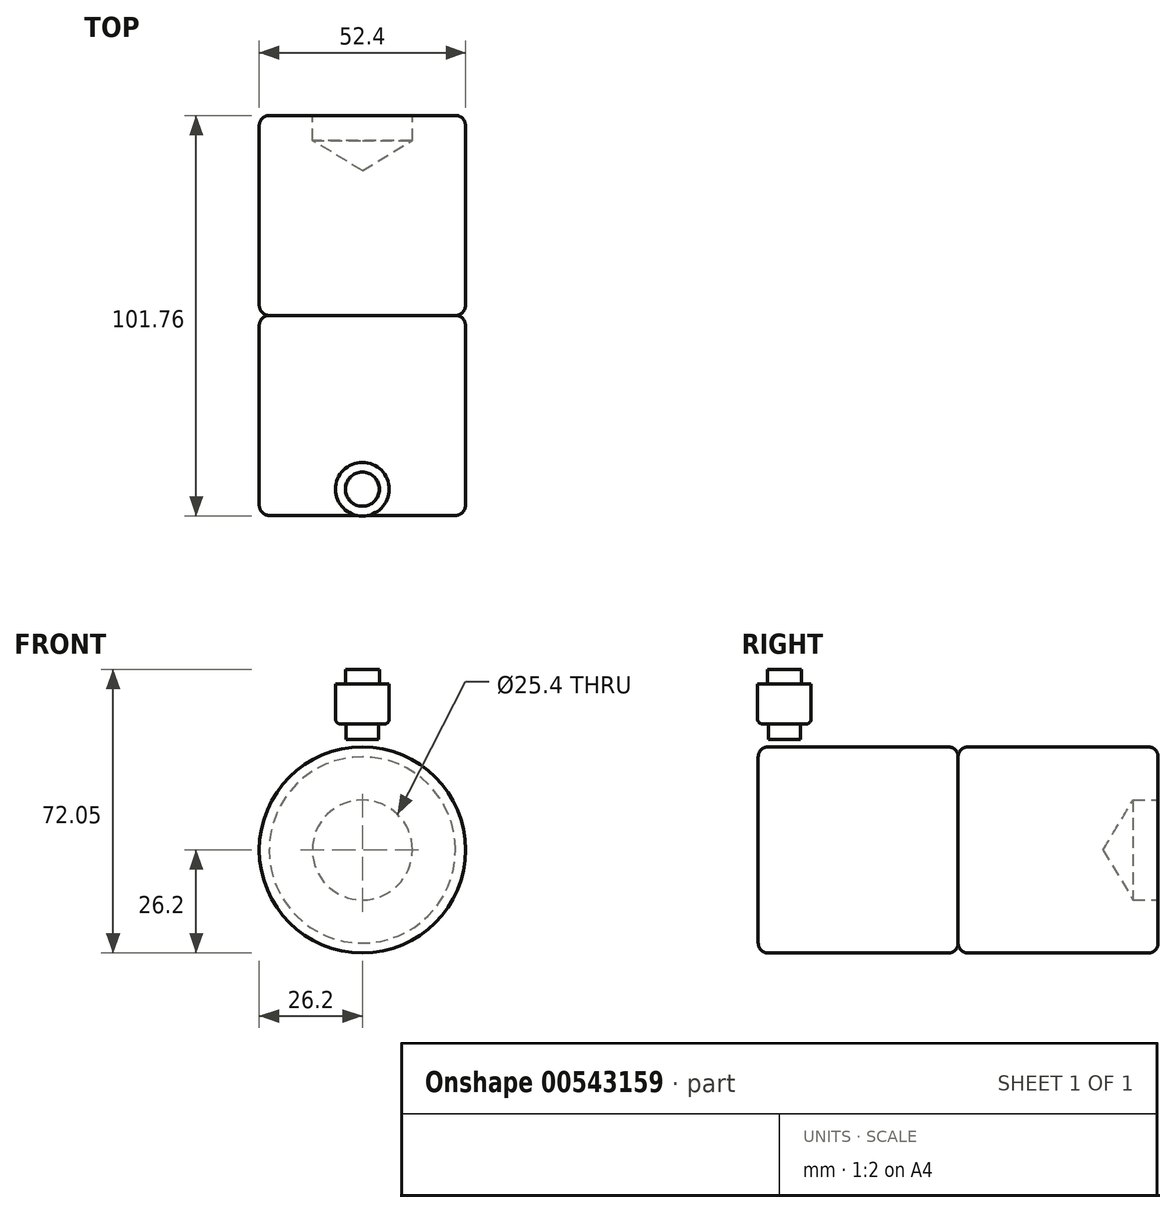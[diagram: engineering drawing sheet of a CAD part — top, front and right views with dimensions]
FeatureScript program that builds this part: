
annotation { "Feature Type Name" : "Feature", "Feature Type Description" : "" }
export const myFeature = defineFeature(function(context is Context, id is Id, definition is map)
    precondition{}
    {
        {
            var Q0;
            Q0=qCreatedBy(makeId("Front.planeOp"),FACE);
            var sketch = newSketch(context, id + "F0", { "sketchPlane" : qUnion([Q0])});
            skCircle(sketch, "E0", {"center": v(0, 0) * mm, "radius": 26.2 * mm});
            skSolve(sketch);
        }
        {
            var Q0;
            Q0=makeQuery(id+"F0.imprint","IMPRINT",FACE,{"disambiguationData":[TD([[makeQuery(id+"F0.imprint","IMPRINT",EDGE,{"derivedFrom":sQuery(id+"F0.wireOp",EDGE,"E0")}),1.0]])]});
            extrude(context, id + "F1", {"entities" : qUnion([Q0]), "oppositeDirection" : true, "depth" : 50.8 * mm, "offsetDistance" : 25.4 * mm});
        }
        {
            var Q0;
            Q0=makeQuery(id+"F1.opExtrude","SWEPT_FACE",FACE,{"disambiguationData":[OSD([sQuery(id+"F0.wireOp",EDGE,"E0")])]});
            fillet(context, id + "F2", {"entities" : qUnion([Q0]), "radius" : 2.54 * mm, "tangentPropagation" : true, "allowEdgeOverflow" : false});
        }
        {
            var Q0;
            Q0=makeQuery(id+"F1.opExtrude","SWEPT_BODY",BODY,{"disambiguationData":[OSD([sQuery(id+"F0.wireOp",EDGE,"E0")])]});
            var Q1;
            Q1=qCreatedBy(makeId("Front.planeOp"),FACE);
            mirror(context, id + "F3", {"operationType" : NewBodyOperationType.ADD, "entities" : qUnion([Q0]), "mirrorPlane" : qUnion([Q1])});
        }
        {
            var Q0;
            Q0=qCreatedBy(makeId("Right.planeOp"),FACE);
            var sketch = newSketch(context, id + "F4", { "sketchPlane" : qUnion([Q0])});
            skLineSegment(sketch, "E1", {"start": v(-44.15, 45.85) * mm, "end": v(-39.81, 45.85) * mm});
            skLineSegment(sketch, "E2", {"start": v(-39.81, 45.85) * mm, "end": v(-39.81, 42.2) * mm});
            skLineSegment(sketch, "E3", {"start": v(-39.81, 42.2) * mm, "end": v(-37.33, 42.2) * mm});
            skLineSegment(sketch, "E4", {"start": v(-37.33, 42.2) * mm, "end": v(-37.33, 31.99) * mm});
            skLineSegment(sketch, "E5", {"start": v(-37.33, 31.99) * mm, "end": v(-40.04, 31.99) * mm});
            skLineSegment(sketch, "E6", {"start": v(-40.04, 31.99) * mm, "end": v(-40.04, 28.04) * mm});
            skLineSegment(sketch, "E7", {"start": v(-40.04, 28.04) * mm, "end": v(-43.46, 28.04) * mm});
            skLineSegment(sketch, "E8", {"start": v(-43.46, 28.04) * mm, "end": v(-44.15, 28.04) * mm});
            skLineSegment(sketch, "E9", {"start": v(-44.15, 28.04) * mm, "end": v(-44.15, 45.85) * mm});
            skSolve(sketch);
        }
        {
            var Q0;
            Q0 = qSketchRegion(id + "F4", true);
            var Q1;
            Q1=sQuery(id+"F4.wireOp",EDGE,"E9");
            revolve(context, id + "F5", {"entities" : qUnion([Q0]), "axis" : qUnion([Q1]), "revolveType" : RevolveType.FULL});
        }
        {
            var Q0;
            Q0=makeQuery(id+"F5.opRevolve","SWEPT_EDGE",EDGE,{"disambiguationData":[OSD([sQuery(id+"F4.wireOp",EDGE,"E4"),sQuery(id+"F4.wireOp",EDGE,"E5")])]});
            fillet(context, id + "F6", {"entities" : qUnion([Q0]), "radius" : 1.27 * mm, "tangentPropagation" : true, "allowEdgeOverflow" : false});
        }
        {
            var Q0;
            Q0=makeQuery(id+"F1.opExtrude","CAP_FACE",FACE,{"disambiguationData":[OSD([sQuery(id+"F0.wireOp",EDGE,"E0")])],"isStart":false});
            var sketch = newSketch(context, id + "F7", { "sketchPlane" : qUnion([Q0])});
            skCircle(sketch, "E10", {"center": v(0, 0) * mm, "radius": 21.92 * mm});
            skSolve(sketch);
        }
        {
            var Q0;
            Q0=sQuery(id+"F7.wireOp",VERTEX,"E10.center");
            var Q1;
            Q1=makeQuery(id+"F1.opExtrude","SWEPT_BODY",BODY,{"disambiguationData":[OSD([sQuery(id+"F0.wireOp",EDGE,"E0")])]});
            hole(context, id + "F8", {"style" : HoleStyle.SIMPLE, "endStyle" : HoleEndStyle.BLIND, "holeDiameter" : 25.4 * mm, "holeDepth" : 6.35 * mm, "isTappedThrough" : true, "tappedDepth" : 12.7 * mm, "tapClearance" : 3, "startFromSketch" : true, "locations" : qUnion([Q0]), "scope" : qUnion([Q1])});
        }
    });
